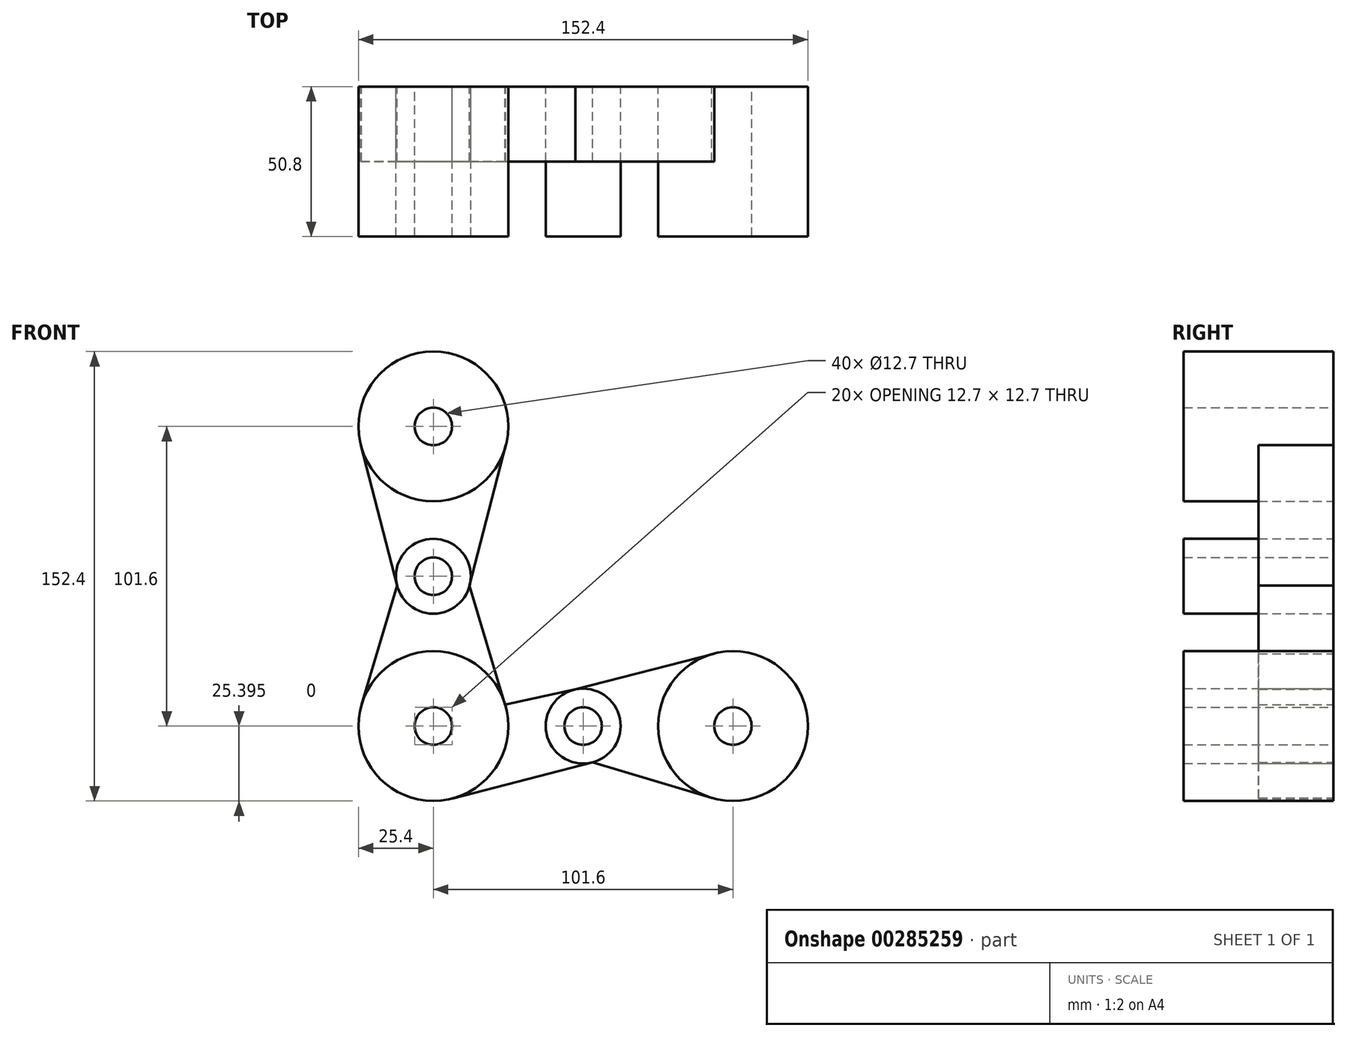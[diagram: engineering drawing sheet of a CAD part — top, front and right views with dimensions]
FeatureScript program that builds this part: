
annotation { "Feature Type Name" : "Feature", "Feature Type Description" : "" }
export const myFeature = defineFeature(function(context is Context, id is Id, definition is map)
    precondition{}
    {
        {
            var Q0;
            Q0=qCreatedBy(makeId("Front.planeOp"),FACE);
            var sketch = newSketch(context, id + "F0", { "sketchPlane" : qUnion([Q0])});
            skLineSegment(sketch, "E0", {"start": v(-101.6, -73.42) * mm, "end": v(-50.8, -73.42) * mm});
            skLineSegment(sketch, "E1", {"start": v(-50.8, -73.42) * mm, "end": v(0, -73.42) * mm});
            skLineSegment(sketch, "E2", {"start": v(-101.6, -73.42) * mm, "end": v(-101.6, -22.62) * mm});
            skLineSegment(sketch, "E3", {"start": v(-101.6, -22.62) * mm, "end": v(-101.6, 28.18) * mm});
            skCircle(sketch, "E4", {"center": v(-101.6, 28.18) * mm, "radius": 25.4 * mm});
            skCircle(sketch, "E5", {"center": v(-101.6, -73.42) * mm, "radius": 25.4 * mm});
            skCircle(sketch, "E6", {"center": v(0, -73.42) * mm, "radius": 25.4 * mm});
            skCircle(sketch, "E7", {"center": v(-101.6, -22.62) * mm, "radius": 12.7 * mm});
            skCircle(sketch, "E8", {"center": v(-50.8, -73.42) * mm, "radius": 12.7 * mm});
            skLineSegment(sketch, "E9", {"start": v(-126.2, 21.83) * mm, "end": v(-113.9, -25.8) * mm});
            skLineSegment(sketch, "E10", {"start": v(-113.9, -25.8) * mm, "end": v(-125.94, -66.16) * mm});
            skLineSegment(sketch, "E11", {"start": v(-77, 21.83) * mm, "end": v(-89.3, -25.8) * mm});
            skLineSegment(sketch, "E12", {"start": v(-89.3, -25.8) * mm, "end": v(-77.26, -66.16) * mm});
            skLineSegment(sketch, "E13", {"start": v(-77.26, -66.16) * mm, "end": v(-53.49, -61.01) * mm});
            skLineSegment(sketch, "E14", {"start": v(-53.49, -61.01) * mm, "end": v(-6.35, -48.83) * mm});
            skLineSegment(sketch, "E15", {"start": v(-95.25, -98.02) * mm, "end": v(-47.63, -85.72) * mm});
            skLineSegment(sketch, "E16", {"start": v(-47.63, -85.72) * mm, "end": v(0, -99.93) * mm});
            skSolve(sketch);
        }
        {
            var Q0;
            {var subQ0=sQuery(id+"F0.wireOp",EDGE,"E4");var subQ1=makeQuery(id+"F0.imprint","INTERSECT",VERTEX,{"derivedFrom":[subQ0,sQuery(id+"F0.wireOp",EDGE,"E9")]});Q0=makeQuery(id+"F0.imprint","IMPRINT",FACE,{"disambiguationData":[TD([[makeQuery(id+"F0.imprint","IMPRINT",EDGE,{"disambiguationData":[TD([[subQ1,-1.0]])],"derivedFrom":subQ0}),1.0]])]});}
            var Q1;
            {var subQ0=sQuery(id+"F0.wireOp",EDGE,"E3");var subQ1=sQuery(id+"F0.wireOp",EDGE,"E2");var subQ2=makeQuery(id+"F0.imprint","INTERSECT",VERTEX,{"derivedFrom":[subQ1,subQ0]});Q1=makeQuery(id+"F0.imprint","IMPRINT",FACE,{"disambiguationData":[TD([[makeQuery(id+"F0.imprint","IMPRINT",EDGE,{"disambiguationData":[TD([[subQ2,1.0]])],"derivedFrom":subQ1}),-1.0]])]});}
            var Q2;
            {var subQ0=sQuery(id+"F0.wireOp",EDGE,"E3");var subQ1=sQuery(id+"F0.wireOp",EDGE,"E2");var subQ2=makeQuery(id+"F0.imprint","INTERSECT",VERTEX,{"derivedFrom":[subQ1,subQ0]});Q2=makeQuery(id+"F0.imprint","IMPRINT",FACE,{"disambiguationData":[TD([[makeQuery(id+"F0.imprint","IMPRINT",EDGE,{"disambiguationData":[TD([[subQ2,1.0]])],"derivedFrom":subQ1}),1.0]])]});}
            var Q3;
            {var subQ0=sQuery(id+"F0.wireOp",EDGE,"E2");var subQ1=sQuery(id+"F0.wireOp",EDGE,"E0");var subQ2=makeQuery(id+"F0.imprint","INTERSECT",VERTEX,{"derivedFrom":[subQ1,subQ0]});Q3=makeQuery(id+"F0.imprint","IMPRINT",FACE,{"disambiguationData":[TD([[makeQuery(id+"F0.imprint","IMPRINT",EDGE,{"disambiguationData":[TD([[subQ2,-1.0]])],"derivedFrom":subQ1}),1.0]])]});}
            var Q4;
            {var subQ3=sQuery(id+"F0.wireOp",EDGE,"E2");var subQ4=sQuery(id+"F0.wireOp",EDGE,"E0");var subQ5=makeQuery(id+"F0.imprint","INTERSECT",VERTEX,{"derivedFrom":[subQ4,subQ3]});Q4=makeQuery(id+"F0.imprint","IMPRINT",FACE,{"disambiguationData":[TD([[makeQuery(id+"F0.imprint","IMPRINT",EDGE,{"disambiguationData":[TD([[subQ5,-1.0]])],"derivedFrom":subQ4}),-1.0]])]});}
            var Q5;
            {var subQ0=sQuery(id+"F0.wireOp",EDGE,"E1");var subQ1=sQuery(id+"F0.wireOp",EDGE,"E0");var subQ2=makeQuery(id+"F0.imprint","INTERSECT",VERTEX,{"derivedFrom":[subQ1,subQ0]});Q5=makeQuery(id+"F0.imprint","IMPRINT",FACE,{"disambiguationData":[TD([[makeQuery(id+"F0.imprint","IMPRINT",EDGE,{"disambiguationData":[TD([[subQ2,1.0]])],"derivedFrom":subQ1}),-1.0]])]});}
            var Q6;
            {var subQ0=sQuery(id+"F0.wireOp",EDGE,"E1");var subQ1=sQuery(id+"F0.wireOp",EDGE,"E0");var subQ2=makeQuery(id+"F0.imprint","INTERSECT",VERTEX,{"derivedFrom":[subQ1,subQ0]});Q6=makeQuery(id+"F0.imprint","IMPRINT",FACE,{"disambiguationData":[TD([[makeQuery(id+"F0.imprint","IMPRINT",EDGE,{"disambiguationData":[TD([[subQ2,1.0]])],"derivedFrom":subQ1}),1.0]])]});}
            var Q7;
            {var subQ0=sQuery(id+"F0.wireOp",EDGE,"E6");var subQ1=makeQuery(id+"F0.imprint","INTERSECT",VERTEX,{"derivedFrom":[subQ0,sQuery(id+"F0.wireOp",EDGE,"E14")]});Q7=makeQuery(id+"F0.imprint","IMPRINT",FACE,{"disambiguationData":[TD([[makeQuery(id+"F0.imprint","IMPRINT",EDGE,{"disambiguationData":[TD([[subQ1,-1.0]])],"derivedFrom":subQ0}),1.0]])]});}
            extrude(context, id + "F1", {"entities" : qUnion([Q0, Q1, Q2, Q3, Q4, Q5, Q6, Q7]), "depth" : 50.8 * mm});
        }
        {
            var Q0;
            {var subQ5=sQuery(id+"F0.wireOp",EDGE,"E9");Q0=makeQuery(id+"F0.imprint","IMPRINT",FACE,{"disambiguationData":[TD([[makeQuery(id+"F0.imprint","IMPRINT",EDGE,{"derivedFrom":subQ5}),1.0]])]});}
            var Q1;
            {var subQ5=sQuery(id+"F0.wireOp",EDGE,"E11");Q1=makeQuery(id+"F0.imprint","IMPRINT",FACE,{"disambiguationData":[TD([[makeQuery(id+"F0.imprint","IMPRINT",EDGE,{"derivedFrom":subQ5}),-1.0]])]});}
            var Q2;
            {var subQ5=sQuery(id+"F0.wireOp",EDGE,"E12");Q2=makeQuery(id+"F0.imprint","IMPRINT",FACE,{"disambiguationData":[TD([[makeQuery(id+"F0.imprint","IMPRINT",EDGE,{"derivedFrom":subQ5}),-1.0]])]});}
            var Q3;
            {var subQ5=sQuery(id+"F0.wireOp",EDGE,"E10");Q3=makeQuery(id+"F0.imprint","IMPRINT",FACE,{"disambiguationData":[TD([[makeQuery(id+"F0.imprint","IMPRINT",EDGE,{"derivedFrom":subQ5}),1.0]])]});}
            var Q4;
            {var subQ5=sQuery(id+"F0.wireOp",EDGE,"E13");Q4=makeQuery(id+"F0.imprint","IMPRINT",FACE,{"disambiguationData":[TD([[makeQuery(id+"F0.imprint","IMPRINT",EDGE,{"derivedFrom":subQ5}),-1.0]])]});}
            var Q5;
            {var subQ5=sQuery(id+"F0.wireOp",EDGE,"E15");Q5=makeQuery(id+"F0.imprint","IMPRINT",FACE,{"disambiguationData":[TD([[makeQuery(id+"F0.imprint","IMPRINT",EDGE,{"derivedFrom":subQ5}),1.0]])]});}
            var Q6;
            {var subQ5=sQuery(id+"F0.wireOp",EDGE,"E14");Q6=makeQuery(id+"F0.imprint","IMPRINT",FACE,{"disambiguationData":[TD([[makeQuery(id+"F0.imprint","IMPRINT",EDGE,{"derivedFrom":subQ5}),-1.0]])]});}
            var Q7;
            {var subQ0=sQuery(id+"F0.wireOp",EDGE,"E6");var subQ1=sQuery(id+"F0.wireOp",EDGE,"E1");var subQ2=makeQuery(id+"F0.imprint","INTERSECT",VERTEX,{"derivedFrom":[subQ1,subQ0]});Q7=makeQuery(id+"F0.imprint","IMPRINT",FACE,{"disambiguationData":[TD([[makeQuery(id+"F0.imprint","IMPRINT",EDGE,{"disambiguationData":[TD([[subQ2,1.0]])],"derivedFrom":subQ1}),-1.0]])]});}
            extrude(context, id + "F2", {"entities" : qUnion([Q0, Q1, Q2, Q3, Q4, Q5, Q6, Q7]), "depth" : 25.4 * mm});
        }
        {
            var Q0;
            Q0=sQuery(id+"F0.wireOp",VERTEX,"E3.end");
            var Q1;
            Q1=sQuery(id+"F0.wireOp",VERTEX,"E7.center");
            var Q2;
            Q2=sQuery(id+"F0.wireOp",VERTEX,"E5.center");
            var Q3;
            Q3=sQuery(id+"F0.wireOp",VERTEX,"E8.center");
            var Q4;
            Q4=sQuery(id+"F0.wireOp",VERTEX,"E1.end");
            var Q5;
            Q5=makeQuery(id+"F1.opExtrude","SWEPT_BODY",BODY,{"disambiguationData":[OSD([sQuery(id+"F0.wireOp",EDGE,"E4")])]});
            var Q6;
            Q6=makeQuery(id+"F1.opExtrude","SWEPT_BODY",BODY,{"disambiguationData":[OSD([sQuery(id+"F0.wireOp",EDGE,"E7")])]});
            var Q7;
            Q7=makeQuery(id+"F1.opExtrude","SWEPT_BODY",BODY,{"disambiguationData":[OSD([sQuery(id+"F0.wireOp",EDGE,"E5")])]});
            var Q8;
            Q8=makeQuery(id+"F1.opExtrude","SWEPT_BODY",BODY,{"disambiguationData":[OSD([sQuery(id+"F0.wireOp",EDGE,"E8")])]});
            var Q9;
            Q9=makeQuery(id+"F1.opExtrude","SWEPT_BODY",BODY,{"disambiguationData":[OSD([sQuery(id+"F0.wireOp",EDGE,"E6")])]});
            hole(context, id + "F3", {"style" : HoleStyle.SIMPLE, "endStyle" : HoleEndStyle.THROUGH, "oppositeDirection" : true, "holeDiameter" : 12.7 * mm, "tappedDepth" : 12.7 * mm, "tapClearance" : 3, "locations" : qUnion([Q0, Q1, Q2, Q3, Q4]), "scope" : qUnion([Q5, Q6, Q7, Q8, Q9])});
        }
    });
